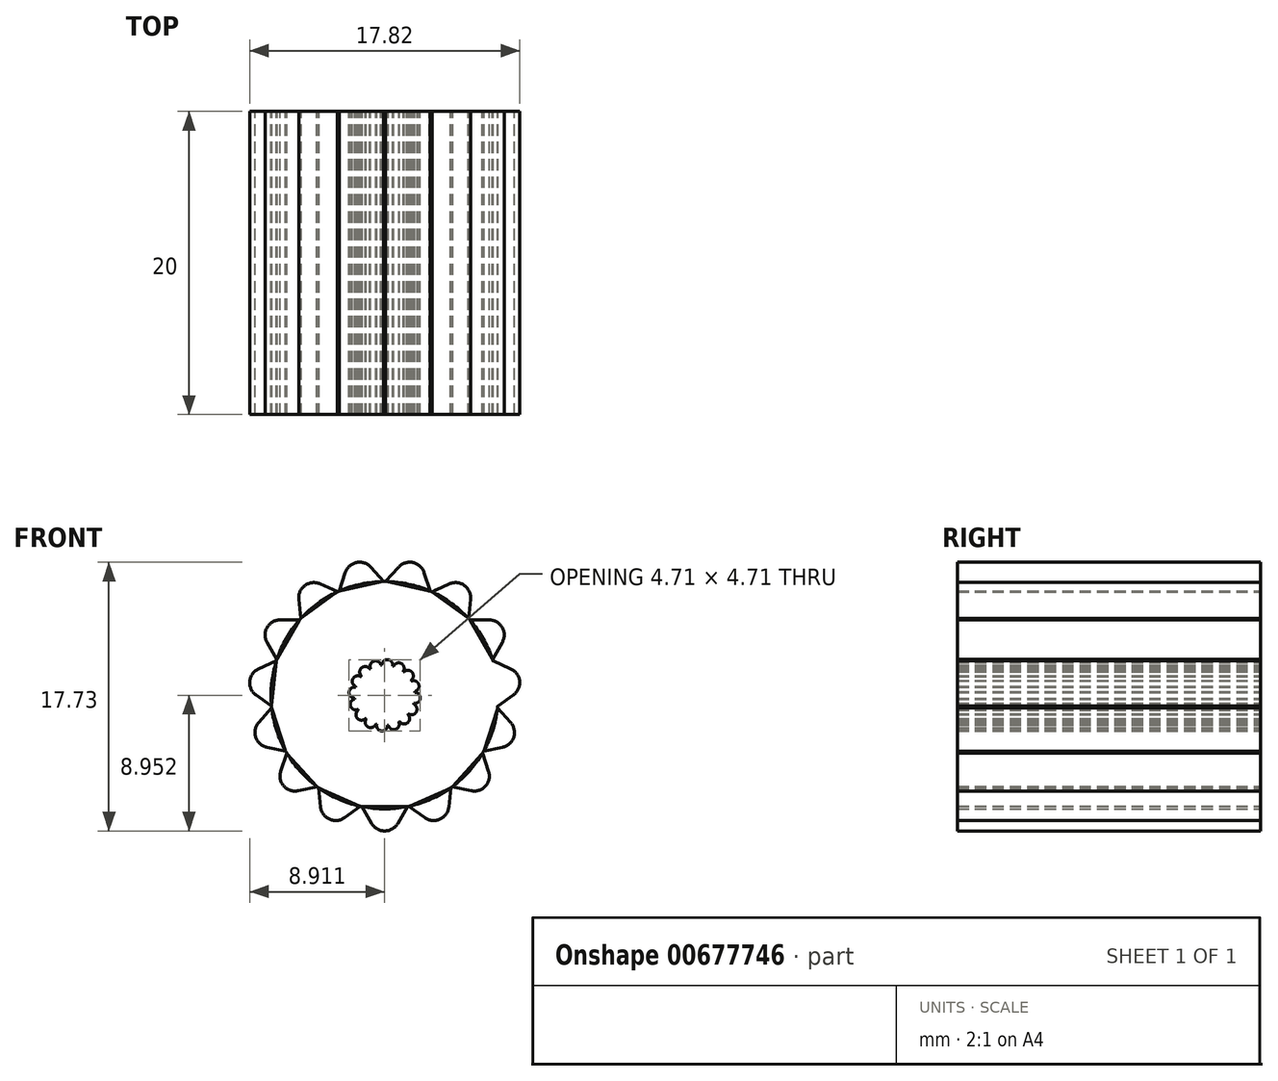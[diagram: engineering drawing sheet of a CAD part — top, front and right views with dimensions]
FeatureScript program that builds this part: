
annotation { "Feature Type Name" : "Feature", "Feature Type Description" : "" }
export const myFeature = defineFeature(function(context is Context, id is Id, definition is map)
    precondition{}
    {
        {
            var Q0;
            Q0=qCreatedBy(makeId("Front.planeOp"),FACE);
            var sketch = newSketch(context, id + "F0", { "sketchPlane" : qUnion([Q0])});
            skCircle(sketch, "E0", {"center": v(-39.12, 44.47) * mm, "radius": 7.5 * mm});
            skCircle(sketch, "E1", {"center": v(-39.12, 44.47) * mm, "radius": 2 * mm});
            skLineSegment(sketch, "E2", {"start": v(-37.62, 37.12) * mm, "end": v(-40.62, 37.12) * mm});
            skLineSegment(sketch, "E3", {"start": v(-40.62, 37.12) * mm, "end": v(-39.12, 34.52) * mm});
            skLineSegment(sketch, "E4", {"start": v(-39.12, 34.52) * mm, "end": v(-37.62, 37.12) * mm});
            skLineSegment(sketch, "E5.1.0", {"start": v(-34.76, 38.36) * mm, "end": v(-37.5, 37.14) * mm});
            skLineSegment(sketch, "E5.1.1", {"start": v(-35.07, 35.38) * mm, "end": v(-34.76, 38.36) * mm});
            skLineSegment(sketch, "E5.1.2", {"start": v(-37.5, 37.14) * mm, "end": v(-35.07, 35.38) * mm});
            skLineSegment(sketch, "E5.2.0", {"start": v(-32.65, 40.66) * mm, "end": v(-34.66, 38.43) * mm});
            skLineSegment(sketch, "E5.2.1", {"start": v(-31.72, 37.81) * mm, "end": v(-32.65, 40.66) * mm});
            skLineSegment(sketch, "E5.2.2", {"start": v(-34.66, 38.43) * mm, "end": v(-31.72, 37.81) * mm});
            skLineSegment(sketch, "E6.3.3.0", {"start": v(-29.65, 41.4) * mm, "end": v(-31.66, 43.63) * mm});
            skLineSegment(sketch, "E6.4.3.0", {"start": v(-31.66, 43.63) * mm, "end": v(-32.59, 40.77) * mm});
            skLineSegment(sketch, "E6.6.3.0", {"start": v(-32.59, 40.77) * mm, "end": v(-29.65, 41.4) * mm});
            skLineSegment(sketch, "E6.3.4.0", {"start": v(-29.22, 45.51) * mm, "end": v(-31.96, 46.73) * mm});
            skLineSegment(sketch, "E6.4.4.0", {"start": v(-31.96, 46.73) * mm, "end": v(-31.65, 43.75) * mm});
            skLineSegment(sketch, "E6.6.4.0", {"start": v(-31.65, 43.75) * mm, "end": v(-29.22, 45.51) * mm});
            skLineSegment(sketch, "E6.3.5.0", {"start": v(-30.5, 49.45) * mm, "end": v(-33.5, 49.45) * mm});
            skLineSegment(sketch, "E6.4.5.0", {"start": v(-33.5, 49.45) * mm, "end": v(-32, 46.85) * mm});
            skLineSegment(sketch, "E6.6.5.0", {"start": v(-32, 46.85) * mm, "end": v(-30.5, 49.45) * mm});
            skLineSegment(sketch, "E6.3.6.0", {"start": v(-33.27, 52.53) * mm, "end": v(-36, 51.3) * mm});
            skLineSegment(sketch, "E6.4.6.0", {"start": v(-36, 51.3) * mm, "end": v(-33.58, 49.54) * mm});
            skLineSegment(sketch, "E6.6.6.0", {"start": v(-33.58, 49.54) * mm, "end": v(-33.27, 52.53) * mm});
            skLineSegment(sketch, "E6.3.7.0", {"start": v(-37.05, 54.2) * mm, "end": v(-39.06, 51.98) * mm});
            skLineSegment(sketch, "E6.4.7.0", {"start": v(-39.06, 51.98) * mm, "end": v(-36.12, 51.36) * mm});
            skLineSegment(sketch, "E6.6.7.0", {"start": v(-36.12, 51.36) * mm, "end": v(-37.05, 54.2) * mm});
            skLineSegment(sketch, "E6.3.8.0", {"start": v(-41.19, 54.2) * mm, "end": v(-42.12, 51.36) * mm});
            skLineSegment(sketch, "E6.4.8.0", {"start": v(-42.12, 51.36) * mm, "end": v(-39.18, 51.98) * mm});
            skLineSegment(sketch, "E6.6.8.0", {"start": v(-39.18, 51.98) * mm, "end": v(-41.19, 54.2) * mm});
            skLineSegment(sketch, "E6.3.9.0", {"start": v(-44.97, 52.53) * mm, "end": v(-44.66, 49.54) * mm});
            skLineSegment(sketch, "E6.4.9.0", {"start": v(-44.66, 49.54) * mm, "end": v(-42.23, 51.3) * mm});
            skLineSegment(sketch, "E6.6.9.0", {"start": v(-42.23, 51.3) * mm, "end": v(-44.97, 52.53) * mm});
            skLineSegment(sketch, "E6.3.10.0", {"start": v(-47.74, 49.45) * mm, "end": v(-46.24, 46.85) * mm});
            skLineSegment(sketch, "E6.4.10.0", {"start": v(-46.24, 46.85) * mm, "end": v(-44.74, 49.45) * mm});
            skLineSegment(sketch, "E6.6.10.0", {"start": v(-44.74, 49.45) * mm, "end": v(-47.74, 49.45) * mm});
            skLineSegment(sketch, "E6.3.11.0", {"start": v(-49.02, 45.51) * mm, "end": v(-46.6, 43.75) * mm});
            skLineSegment(sketch, "E6.4.11.0", {"start": v(-46.6, 43.75) * mm, "end": v(-46.28, 46.73) * mm});
            skLineSegment(sketch, "E6.6.11.0", {"start": v(-46.28, 46.73) * mm, "end": v(-49.02, 45.51) * mm});
            skLineSegment(sketch, "E6.3.12.0", {"start": v(-48.59, 41.4) * mm, "end": v(-45.65, 40.77) * mm});
            skLineSegment(sketch, "E6.4.12.0", {"start": v(-45.65, 40.77) * mm, "end": v(-46.58, 43.63) * mm});
            skLineSegment(sketch, "E6.6.12.0", {"start": v(-46.58, 43.63) * mm, "end": v(-48.59, 41.4) * mm});
            skLineSegment(sketch, "E6.3.13.0", {"start": v(-46.52, 37.81) * mm, "end": v(-43.58, 38.43) * mm});
            skLineSegment(sketch, "E6.4.13.0", {"start": v(-43.58, 38.43) * mm, "end": v(-45.59, 40.66) * mm});
            skLineSegment(sketch, "E6.6.13.0", {"start": v(-45.59, 40.66) * mm, "end": v(-46.52, 37.81) * mm});
            skLineSegment(sketch, "E6.3.14.0", {"start": v(-43.17, 35.38) * mm, "end": v(-40.74, 37.14) * mm});
            skLineSegment(sketch, "E6.4.14.0", {"start": v(-40.74, 37.14) * mm, "end": v(-43.48, 38.36) * mm});
            skLineSegment(sketch, "E6.6.14.0", {"start": v(-43.48, 38.36) * mm, "end": v(-43.17, 35.38) * mm});
            skCircle(sketch, "E7", {"center": v(-37.21, 45.07) * mm, "radius": 0.36 * mm});
            skCircle(sketch, "E8.1.0", {"center": v(-37.59, 45.76) * mm, "radius": 0.36 * mm});
            skCircle(sketch, "E8.2.0", {"center": v(-38.2, 46.25) * mm, "radius": 0.36 * mm});
            skCircle(sketch, "E8.3.0", {"center": v(-38.95, 46.46) * mm, "radius": 0.36 * mm});
            skCircle(sketch, "E8.4.0", {"center": v(-39.72, 46.38) * mm, "radius": 0.36 * mm});
            skCircle(sketch, "E8.5.0", {"center": v(-40.4, 46) * mm, "radius": 0.36 * mm});
            skCircle(sketch, "E8.6.0", {"center": v(-40.9, 45.4) * mm, "radius": 0.36 * mm});
            skCircle(sketch, "E8.7.0", {"center": v(-41.11, 44.65) * mm, "radius": 0.36 * mm});
            skCircle(sketch, "E8.8.0", {"center": v(-41.03, 43.87) * mm, "radius": 0.36 * mm});
            skCircle(sketch, "E8.9.0", {"center": v(-40.65, 43.19) * mm, "radius": 0.36 * mm});
            skCircle(sketch, "E8.10.0", {"center": v(-40.04, 42.7) * mm, "radius": 0.36 * mm});
            skCircle(sketch, "E8.11.0", {"center": v(-39.3, 42.48) * mm, "radius": 0.36 * mm});
            skCircle(sketch, "E8.12.0", {"center": v(-38.52, 42.56) * mm, "radius": 0.36 * mm});
            skCircle(sketch, "E8.13.0", {"center": v(-37.83, 42.94) * mm, "radius": 0.36 * mm});
            skCircle(sketch, "E8.14.0", {"center": v(-37.34, 43.55) * mm, "radius": 0.36 * mm});
            skCircle(sketch, "E8.15.0", {"center": v(-37.13, 44.3) * mm, "radius": 0.36 * mm});
            skSolve(sketch);
        }
        {
            var Q0;
            {var subQ0=sQuery(id+"F0.wireOp",EDGE,"E5.2.1");Q0=makeQuery(id+"F0.imprint","IMPRINT",FACE,{"disambiguationData":[TD([[makeQuery(id+"F0.imprint","IMPRINT",EDGE,{"derivedFrom":subQ0}),1.0]])]});}
            var Q1;
            {var subQ0=sQuery(id+"F0.wireOp",EDGE,"E3");Q1=makeQuery(id+"F0.imprint","IMPRINT",FACE,{"disambiguationData":[TD([[makeQuery(id+"F0.imprint","IMPRINT",EDGE,{"derivedFrom":subQ0}),1.0]])]});}
            var Q2;
            {var subQ1=sQuery(id+"F0.wireOp",EDGE,"E6.3.14.0");Q2=makeQuery(id+"F0.imprint","IMPRINT",FACE,{"disambiguationData":[TD([[makeQuery(id+"F0.imprint","IMPRINT",EDGE,{"derivedFrom":subQ1}),1.0]])]});}
            var Q3;
            {var subQ0=sQuery(id+"F0.wireOp",EDGE,"E5.1.1");Q3=makeQuery(id+"F0.imprint","IMPRINT",FACE,{"disambiguationData":[TD([[makeQuery(id+"F0.imprint","IMPRINT",EDGE,{"derivedFrom":subQ0}),1.0]])]});}
            var Q4;
            {var subQ4=sQuery(id+"F0.wireOp",EDGE,"E6.3.13.0");Q4=makeQuery(id+"F0.imprint","IMPRINT",FACE,{"disambiguationData":[TD([[makeQuery(id+"F0.imprint","IMPRINT",EDGE,{"derivedFrom":subQ4}),1.0]])]});}
            var Q5;
            {var subQ4=sQuery(id+"F0.wireOp",EDGE,"E6.3.12.0");Q5=makeQuery(id+"F0.imprint","IMPRINT",FACE,{"disambiguationData":[TD([[makeQuery(id+"F0.imprint","IMPRINT",EDGE,{"derivedFrom":subQ4}),1.0]])]});}
            var Q6;
            {var subQ4=sQuery(id+"F0.wireOp",EDGE,"E6.3.11.0");Q6=makeQuery(id+"F0.imprint","IMPRINT",FACE,{"disambiguationData":[TD([[makeQuery(id+"F0.imprint","IMPRINT",EDGE,{"derivedFrom":subQ4}),1.0]])]});}
            var Q7;
            {var subQ4=sQuery(id+"F0.wireOp",EDGE,"E6.3.10.0");Q7=makeQuery(id+"F0.imprint","IMPRINT",FACE,{"disambiguationData":[TD([[makeQuery(id+"F0.imprint","IMPRINT",EDGE,{"derivedFrom":subQ4}),1.0]])]});}
            var Q8;
            {var subQ1=sQuery(id+"F0.wireOp",EDGE,"E6.3.9.0");Q8=makeQuery(id+"F0.imprint","IMPRINT",FACE,{"disambiguationData":[TD([[makeQuery(id+"F0.imprint","IMPRINT",EDGE,{"derivedFrom":subQ1}),1.0]])]});}
            var Q9;
            {var subQ4=sQuery(id+"F0.wireOp",EDGE,"E6.3.8.0");Q9=makeQuery(id+"F0.imprint","IMPRINT",FACE,{"disambiguationData":[TD([[makeQuery(id+"F0.imprint","IMPRINT",EDGE,{"derivedFrom":subQ4}),1.0]])]});}
            var Q10;
            {var subQ4=sQuery(id+"F0.wireOp",EDGE,"E6.3.7.0");Q10=makeQuery(id+"F0.imprint","IMPRINT",FACE,{"disambiguationData":[TD([[makeQuery(id+"F0.imprint","IMPRINT",EDGE,{"derivedFrom":subQ4}),1.0]])]});}
            var Q11;
            {var subQ4=sQuery(id+"F0.wireOp",EDGE,"E6.3.6.0");Q11=makeQuery(id+"F0.imprint","IMPRINT",FACE,{"disambiguationData":[TD([[makeQuery(id+"F0.imprint","IMPRINT",EDGE,{"derivedFrom":subQ4}),1.0]])]});}
            var Q12;
            {var subQ4=sQuery(id+"F0.wireOp",EDGE,"E6.3.5.0");Q12=makeQuery(id+"F0.imprint","IMPRINT",FACE,{"disambiguationData":[TD([[makeQuery(id+"F0.imprint","IMPRINT",EDGE,{"derivedFrom":subQ4}),1.0]])]});}
            var Q13;
            {var subQ1=sQuery(id+"F0.wireOp",EDGE,"E6.3.4.0");Q13=makeQuery(id+"F0.imprint","IMPRINT",FACE,{"disambiguationData":[TD([[makeQuery(id+"F0.imprint","IMPRINT",EDGE,{"derivedFrom":subQ1}),1.0]])]});}
            var Q14;
            {var subQ5=sQuery(id+"F0.wireOp",EDGE,"E6.3.3.0");Q14=makeQuery(id+"F0.imprint","IMPRINT",FACE,{"disambiguationData":[TD([[makeQuery(id+"F0.imprint","IMPRINT",EDGE,{"derivedFrom":subQ5}),1.0]])]});}
            var Q15;
            {var subQ0=sQuery(id+"F0.wireOp",EDGE,"E6.4.3.0");var subQ1=sQuery(id+"F0.wireOp",EDGE,"E0");var subQ2=makeQuery(id+"F0.imprint","INTERSECT",VERTEX,{"disambiguationData":[OD(0.0)],"derivedFrom":[subQ1,subQ0]});Q15=makeQuery(id+"F0.imprint","IMPRINT",FACE,{"disambiguationData":[TD([[makeQuery(id+"F0.imprint","IMPRINT",EDGE,{"disambiguationData":[TD([[subQ2,-1.0]])],"derivedFrom":subQ1}),1.0]])]});}
            var Q16;
            Q16=makeQuery(id+"F0.imprint","IMPRINT",FACE,{"disambiguationData":[TD([[makeQuery(id+"F0.imprint","IMPRINT",EDGE,{"derivedFrom":sQuery(id+"F0.wireOp",EDGE,"E1")}),-1.0]])]});
            var Q17;
            {var subQ0=sQuery(id+"F0.wireOp",EDGE,"E6.4.12.0");var subQ1=sQuery(id+"F0.wireOp",EDGE,"E0");var subQ2=makeQuery(id+"F0.imprint","INTERSECT",VERTEX,{"disambiguationData":[OD(0.0)],"derivedFrom":[subQ1,subQ0]});Q17=makeQuery(id+"F0.imprint","IMPRINT",FACE,{"disambiguationData":[TD([[makeQuery(id+"F0.imprint","IMPRINT",EDGE,{"disambiguationData":[TD([[subQ2,-1.0]])],"derivedFrom":subQ1}),1.0]])]});}
            var Q18;
            {var subQ0=sQuery(id+"F0.wireOp",EDGE,"E6.4.6.0");var subQ1=sQuery(id+"F0.wireOp",EDGE,"E0");var subQ2=makeQuery(id+"F0.imprint","INTERSECT",VERTEX,{"disambiguationData":[OD(0.0)],"derivedFrom":[subQ1,subQ0]});Q18=makeQuery(id+"F0.imprint","IMPRINT",FACE,{"disambiguationData":[TD([[makeQuery(id+"F0.imprint","IMPRINT",EDGE,{"disambiguationData":[TD([[subQ2,-1.0]])],"derivedFrom":subQ1}),1.0]])]});}
            var Q19;
            {var subQ0=sQuery(id+"F0.wireOp",EDGE,"E6.4.7.0");var subQ1=sQuery(id+"F0.wireOp",EDGE,"E0");var subQ2=makeQuery(id+"F0.imprint","INTERSECT",VERTEX,{"disambiguationData":[OD(0.0)],"derivedFrom":[subQ1,subQ0]});Q19=makeQuery(id+"F0.imprint","IMPRINT",FACE,{"disambiguationData":[TD([[makeQuery(id+"F0.imprint","IMPRINT",EDGE,{"disambiguationData":[TD([[subQ2,-1.0]])],"derivedFrom":subQ1}),1.0]])]});}
            var Q20;
            {var subQ0=sQuery(id+"F0.wireOp",EDGE,"E6.4.13.0");var subQ1=sQuery(id+"F0.wireOp",EDGE,"E0");var subQ2=makeQuery(id+"F0.imprint","INTERSECT",VERTEX,{"disambiguationData":[OD(0.0)],"derivedFrom":[subQ1,subQ0]});Q20=makeQuery(id+"F0.imprint","IMPRINT",FACE,{"disambiguationData":[TD([[makeQuery(id+"F0.imprint","IMPRINT",EDGE,{"disambiguationData":[TD([[subQ2,-1.0]])],"derivedFrom":subQ1}),1.0]])]});}
            var Q21;
            {var subQ0=sQuery(id+"F0.wireOp",EDGE,"E6.4.5.0");var subQ1=sQuery(id+"F0.wireOp",EDGE,"E0");var subQ2=makeQuery(id+"F0.imprint","INTERSECT",VERTEX,{"disambiguationData":[OD(0.0)],"derivedFrom":[subQ1,subQ0]});Q21=makeQuery(id+"F0.imprint","IMPRINT",FACE,{"disambiguationData":[TD([[makeQuery(id+"F0.imprint","IMPRINT",EDGE,{"disambiguationData":[TD([[subQ2,-1.0]])],"derivedFrom":subQ1}),1.0]])]});}
            var Q22;
            {var subQ0=sQuery(id+"F0.wireOp",EDGE,"E6.4.11.0");var subQ1=sQuery(id+"F0.wireOp",EDGE,"E0");var subQ2=makeQuery(id+"F0.imprint","INTERSECT",VERTEX,{"disambiguationData":[OD(0.0)],"derivedFrom":[subQ1,subQ0]});Q22=makeQuery(id+"F0.imprint","IMPRINT",FACE,{"disambiguationData":[TD([[makeQuery(id+"F0.imprint","IMPRINT",EDGE,{"disambiguationData":[TD([[subQ2,-1.0]])],"derivedFrom":subQ1}),1.0]])]});}
            var Q23;
            {var subQ0=sQuery(id+"F0.wireOp",EDGE,"E5.2.0");var subQ1=sQuery(id+"F0.wireOp",EDGE,"E0");var subQ2=makeQuery(id+"F0.imprint","INTERSECT",VERTEX,{"disambiguationData":[OD(0.0)],"derivedFrom":[subQ1,subQ0]});Q23=makeQuery(id+"F0.imprint","IMPRINT",FACE,{"disambiguationData":[TD([[makeQuery(id+"F0.imprint","IMPRINT",EDGE,{"disambiguationData":[TD([[subQ2,-1.0]])],"derivedFrom":subQ1}),1.0]])]});}
            var Q24;
            {var subQ0=sQuery(id+"F0.wireOp",EDGE,"E6.4.4.0");var subQ1=sQuery(id+"F0.wireOp",EDGE,"E0");var subQ2=makeQuery(id+"F0.imprint","INTERSECT",VERTEX,{"disambiguationData":[OD(0.0)],"derivedFrom":[subQ1,subQ0]});Q24=makeQuery(id+"F0.imprint","IMPRINT",FACE,{"disambiguationData":[TD([[makeQuery(id+"F0.imprint","IMPRINT",EDGE,{"disambiguationData":[TD([[subQ2,1.0]])],"derivedFrom":subQ1}),1.0]])]});}
            var Q25;
            {var subQ0=sQuery(id+"F0.wireOp",EDGE,"E2");var subQ1=sQuery(id+"F0.wireOp",EDGE,"E0");var subQ2=makeQuery(id+"F0.imprint","INTERSECT",VERTEX,{"disambiguationData":[OD(0.0)],"derivedFrom":[subQ1,subQ0]});Q25=makeQuery(id+"F0.imprint","IMPRINT",FACE,{"disambiguationData":[TD([[makeQuery(id+"F0.imprint","IMPRINT",EDGE,{"disambiguationData":[TD([[subQ2,-1.0]])],"derivedFrom":subQ1}),1.0]])]});}
            var Q26;
            {var subQ0=sQuery(id+"F0.wireOp",EDGE,"E6.4.9.0");var subQ1=sQuery(id+"F0.wireOp",EDGE,"E0");var subQ2=makeQuery(id+"F0.imprint","INTERSECT",VERTEX,{"disambiguationData":[OD(0.0)],"derivedFrom":[subQ1,subQ0]});Q26=makeQuery(id+"F0.imprint","IMPRINT",FACE,{"disambiguationData":[TD([[makeQuery(id+"F0.imprint","IMPRINT",EDGE,{"disambiguationData":[TD([[subQ2,-1.0]])],"derivedFrom":subQ1}),1.0]])]});}
            var Q27;
            {var subQ0=sQuery(id+"F0.wireOp",EDGE,"E6.4.8.0");var subQ1=sQuery(id+"F0.wireOp",EDGE,"E0");var subQ2=makeQuery(id+"F0.imprint","INTERSECT",VERTEX,{"disambiguationData":[OD(0.0)],"derivedFrom":[subQ1,subQ0]});Q27=makeQuery(id+"F0.imprint","IMPRINT",FACE,{"disambiguationData":[TD([[makeQuery(id+"F0.imprint","IMPRINT",EDGE,{"disambiguationData":[TD([[subQ2,-1.0]])],"derivedFrom":subQ1}),1.0]])]});}
            var Q28;
            {var subQ0=sQuery(id+"F0.wireOp",EDGE,"E6.4.10.0");var subQ1=sQuery(id+"F0.wireOp",EDGE,"E0");var subQ2=makeQuery(id+"F0.imprint","INTERSECT",VERTEX,{"disambiguationData":[OD(0.0)],"derivedFrom":[subQ1,subQ0]});Q28=makeQuery(id+"F0.imprint","IMPRINT",FACE,{"disambiguationData":[TD([[makeQuery(id+"F0.imprint","IMPRINT",EDGE,{"disambiguationData":[TD([[subQ2,-1.0]])],"derivedFrom":subQ1}),1.0]])]});}
            var Q29;
            {var subQ0=sQuery(id+"F0.wireOp",EDGE,"E5.1.0");var subQ1=sQuery(id+"F0.wireOp",EDGE,"E0");var subQ2=makeQuery(id+"F0.imprint","INTERSECT",VERTEX,{"disambiguationData":[OD(0.0)],"derivedFrom":[subQ1,subQ0]});Q29=makeQuery(id+"F0.imprint","IMPRINT",FACE,{"disambiguationData":[TD([[makeQuery(id+"F0.imprint","IMPRINT",EDGE,{"disambiguationData":[TD([[subQ2,-1.0]])],"derivedFrom":subQ1}),1.0]])]});}
            var Q30;
            {var subQ0=sQuery(id+"F0.wireOp",EDGE,"E6.4.14.0");var subQ1=sQuery(id+"F0.wireOp",EDGE,"E0");var subQ2=makeQuery(id+"F0.imprint","INTERSECT",VERTEX,{"disambiguationData":[OD(0.0)],"derivedFrom":[subQ1,subQ0]});Q30=makeQuery(id+"F0.imprint","IMPRINT",FACE,{"disambiguationData":[TD([[makeQuery(id+"F0.imprint","IMPRINT",EDGE,{"disambiguationData":[TD([[subQ2,-1.0]])],"derivedFrom":subQ1}),1.0]])]});}
            extrude(context, id + "F1", {"entities" : qUnion([Q0, Q1, Q2, Q3, Q4, Q5, Q6, Q7, Q8, Q9, Q10, Q11, Q12, Q13, Q14, Q15, Q16, Q17, Q18, Q19, Q20, Q21, Q22, Q23, Q24, Q25, Q26, Q27, Q28, Q29, Q30]), "depth" : 20 * mm, "offsetDistance" : 25 * mm});
        }
        {
            var Q0;
            Q0=makeQuery(id+"F1.opExtrude","SWEPT_EDGE",EDGE,{"disambiguationData":[OSD([sQuery(id+"F0.wireOp",EDGE,"E6.3.5.0"),sQuery(id+"F0.wireOp",EDGE,"E6.6.5.0")])]});
            var Q1;
            Q1=makeQuery(id+"F1.opExtrude","SWEPT_EDGE",EDGE,{"disambiguationData":[OSD([sQuery(id+"F0.wireOp",EDGE,"E6.3.4.0"),sQuery(id+"F0.wireOp",EDGE,"E6.6.4.0")])]});
            var Q2;
            Q2=makeQuery(id+"F1.opExtrude","SWEPT_EDGE",EDGE,{"disambiguationData":[OSD([sQuery(id+"F0.wireOp",EDGE,"E6.3.3.0"),sQuery(id+"F0.wireOp",EDGE,"E6.6.3.0")])]});
            var Q3;
            Q3=makeQuery(id+"F1.opExtrude","SWEPT_EDGE",EDGE,{"disambiguationData":[OSD([sQuery(id+"F0.wireOp",EDGE,"E5.2.1"),sQuery(id+"F0.wireOp",EDGE,"E5.2.2")])]});
            var Q4;
            Q4=makeQuery(id+"F1.opExtrude","SWEPT_EDGE",EDGE,{"disambiguationData":[OSD([sQuery(id+"F0.wireOp",EDGE,"E5.1.1"),sQuery(id+"F0.wireOp",EDGE,"E5.1.2")])]});
            var Q5;
            Q5=makeQuery(id+"F1.opExtrude","SWEPT_EDGE",EDGE,{"disambiguationData":[OSD([sQuery(id+"F0.wireOp",EDGE,"E3"),sQuery(id+"F0.wireOp",EDGE,"E4")])]});
            var Q6;
            Q6=makeQuery(id+"F1.opExtrude","SWEPT_EDGE",EDGE,{"disambiguationData":[OSD([sQuery(id+"F0.wireOp",EDGE,"E6.3.14.0"),sQuery(id+"F0.wireOp",EDGE,"E6.6.14.0")])]});
            var Q7;
            Q7=makeQuery(id+"F1.opExtrude","SWEPT_EDGE",EDGE,{"disambiguationData":[OSD([sQuery(id+"F0.wireOp",EDGE,"E6.3.13.0"),sQuery(id+"F0.wireOp",EDGE,"E6.6.13.0")])]});
            var Q8;
            Q8=makeQuery(id+"F1.opExtrude","SWEPT_EDGE",EDGE,{"disambiguationData":[OSD([sQuery(id+"F0.wireOp",EDGE,"E6.3.6.0"),sQuery(id+"F0.wireOp",EDGE,"E6.6.6.0")])]});
            var Q9;
            Q9=makeQuery(id+"F1.opExtrude","SWEPT_EDGE",EDGE,{"disambiguationData":[OSD([sQuery(id+"F0.wireOp",EDGE,"E6.3.6.0"),sQuery(id+"F0.wireOp",EDGE,"E6.4.6.0")])]});
            var Q10;
            Q10=makeQuery(id+"F1.opExtrude","SWEPT_EDGE",EDGE,{"disambiguationData":[OSD([sQuery(id+"F0.wireOp",EDGE,"E6.3.8.0"),sQuery(id+"F0.wireOp",EDGE,"E6.6.8.0")])]});
            var Q11;
            Q11=makeQuery(id+"F1.opExtrude","SWEPT_EDGE",EDGE,{"disambiguationData":[OSD([sQuery(id+"F0.wireOp",EDGE,"E6.3.9.0"),sQuery(id+"F0.wireOp",EDGE,"E6.6.9.0")])]});
            var Q12;
            Q12=makeQuery(id+"F1.opExtrude","SWEPT_EDGE",EDGE,{"disambiguationData":[OSD([sQuery(id+"F0.wireOp",EDGE,"E6.3.10.0"),sQuery(id+"F0.wireOp",EDGE,"E6.6.10.0")])]});
            var Q13;
            Q13=makeQuery(id+"F1.opExtrude","SWEPT_EDGE",EDGE,{"disambiguationData":[OSD([sQuery(id+"F0.wireOp",EDGE,"E6.3.11.0"),sQuery(id+"F0.wireOp",EDGE,"E6.6.11.0")])]});
            var Q14;
            Q14=makeQuery(id+"F1.opExtrude","SWEPT_EDGE",EDGE,{"disambiguationData":[OSD([sQuery(id+"F0.wireOp",EDGE,"E6.3.12.0"),sQuery(id+"F0.wireOp",EDGE,"E6.6.12.0")])]});
            var Q15;
            Q15=makeQuery(id+"F1.opExtrude","SWEPT_EDGE",EDGE,{"disambiguationData":[OSD([sQuery(id+"F0.wireOp",EDGE,"E6.3.7.0"),sQuery(id+"F0.wireOp",EDGE,"E6.6.7.0")])]});
            fillet(context, id + "F2", {"entities" : qUnion([Q0, Q1, Q2, Q3, Q4, Q5, Q6, Q7, Q8, Q9, Q10, Q11, Q12, Q13, Q14, Q15]), "radius" : 1 * mm, "tangentPropagation" : true, "allowEdgeOverflow" : false});
        }
    });
